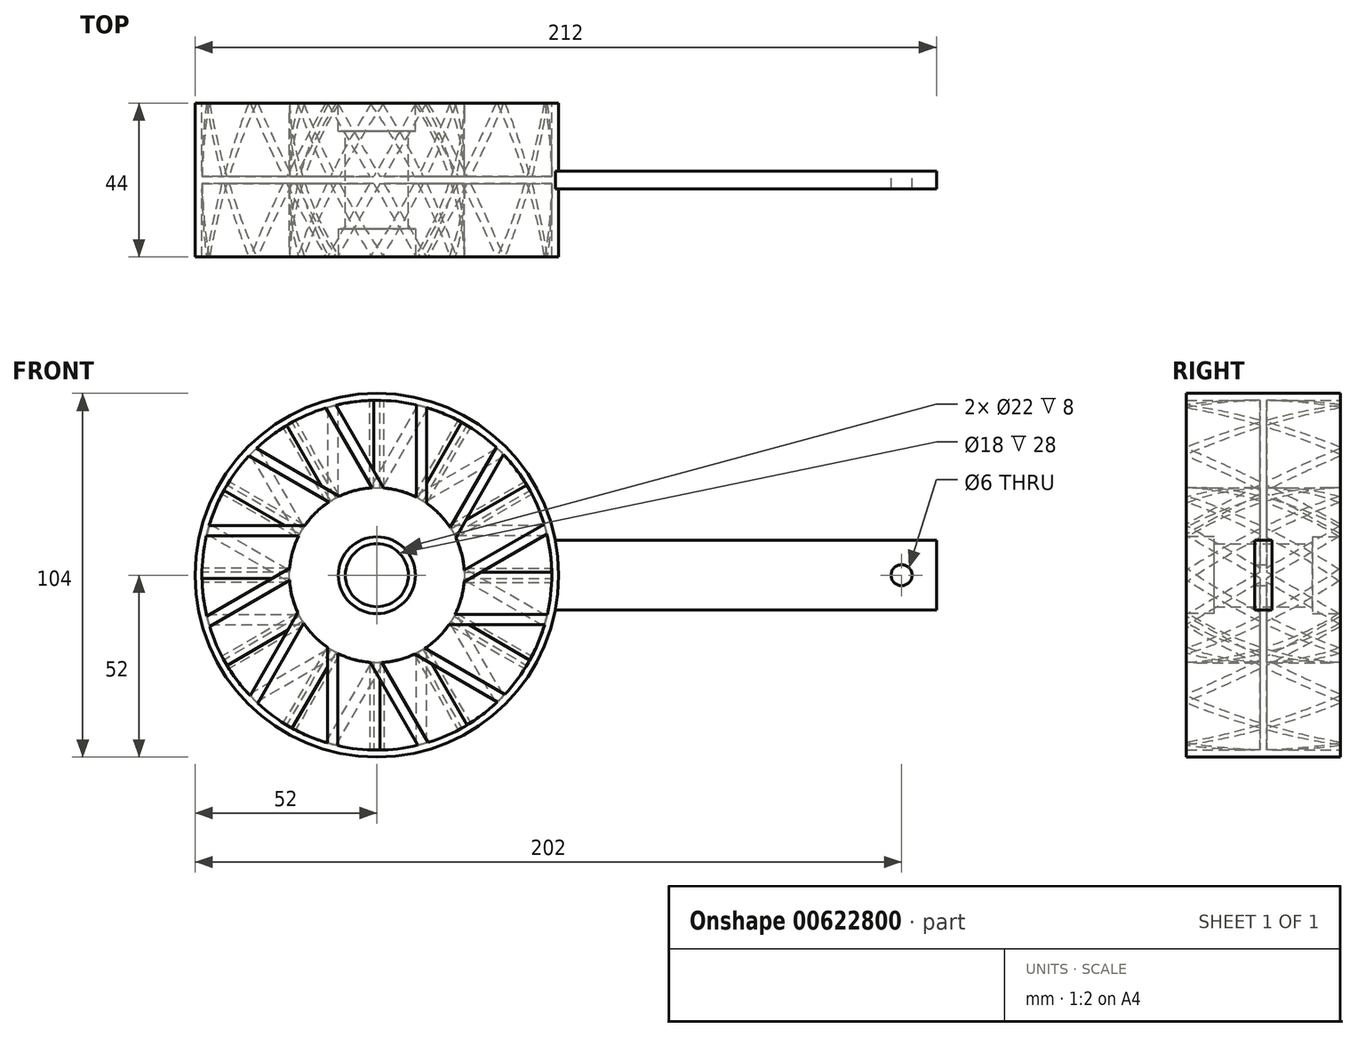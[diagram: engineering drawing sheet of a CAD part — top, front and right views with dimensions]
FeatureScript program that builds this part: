
annotation { "Feature Type Name" : "Feature", "Feature Type Description" : "" }
export const myFeature = defineFeature(function(context is Context, id is Id, definition is map)
    precondition{}
    {
        {
            var Q0;
            Q0=qCreatedBy(makeId("Front.planeOp"),FACE);
            var sketch = newSketch(context, id + "F0", { "sketchPlane" : qUnion([Q0])});
            skCircle(sketch, "E0", {"center": v(0, 0) * mm, "radius": 50 * mm});
            skCircle(sketch, "E1.0", {"center": v(0, 0) * mm, "radius": 52 * mm});
            skCircle(sketch, "E2", {"center": v(0, 0) * mm, "radius": 25 * mm});
            skCircle(sketch, "E3.0", {"center": v(0, 0) * mm, "radius": 23 * mm});
            skLineSegment(sketch, "E4", {"start": v(-23, 0) * mm, "end": v(-50, 0) * mm, "construction": true});
            skLineSegment(sketch, "E5.bottom", {"start": v(-57.83, -1.26) * mm, "end": v(-15.17, -1.26) * mm});
            skLineSegment(sketch, "E5.top", {"start": v(-57.83, 1.26) * mm, "end": v(-15.17, 1.26) * mm});
            skLineSegment(sketch, "E5.left", {"start": v(-57.83, -1.26) * mm, "end": v(-57.83, 1.26) * mm});
            skLineSegment(sketch, "E5.right", {"start": v(-15.17, -1.26) * mm, "end": v(-15.17, 1.26) * mm});
            skPoint(sketch, "E5.middle", {"position": v(-36.5, 0) * mm});
            skCircle(sketch, "E6", {"center": v(0, 0) * mm, "radius": 77.5 * mm});
            skCircle(sketch, "E7", {"center": v(0, 0) * mm, "radius": 9 * mm});
            skLineSegment(sketch, "E8", {"start": v(51.03, 10) * mm, "end": v(160, 10) * mm});
            skLineSegment(sketch, "E9", {"start": v(160, 10) * mm, "end": v(160, -10) * mm});
            skLineSegment(sketch, "E10", {"start": v(160, -10) * mm, "end": v(51.03, -10) * mm});
            skCircle(sketch, "E11", {"center": v(150, 0) * mm, "radius": 3 * mm});
            skSolve(sketch);
        }
        {
            var Q0;
            {var subQ0=sQuery(id+"F0.wireOp",EDGE,"E5.bottom");var subQ1=sQuery(id+"F0.wireOp",EDGE,"E0");var subQ2=makeQuery(id+"F0.imprint","INTERSECT",VERTEX,{"derivedFrom":[subQ1,subQ0]});Q0=makeQuery(id+"F0.imprint","IMPRINT",FACE,{"disambiguationData":[TD([[makeQuery(id+"F0.imprint","IMPRINT",EDGE,{"disambiguationData":[TD([[subQ2,-1.0]])],"derivedFrom":subQ1}),-1.0]])]});}
            var Q1;
            {var subQ0=sQuery(id+"F0.wireOp",EDGE,"E5.bottom");var subQ1=sQuery(id+"F0.wireOp",EDGE,"E0");var subQ2=makeQuery(id+"F0.imprint","INTERSECT",VERTEX,{"derivedFrom":[subQ1,subQ0]});Q1=makeQuery(id+"F0.imprint","IMPRINT",FACE,{"disambiguationData":[TD([[makeQuery(id+"F0.imprint","IMPRINT",EDGE,{"disambiguationData":[TD([[subQ2,1.0]])],"derivedFrom":subQ1}),-1.0]])]});}
            extrude(context, id + "F1", {"entities" : qUnion([Q0, Q1]), "depth" : 22 * mm, "offsetDistance" : 25 * mm, "hasSecondDirection" : true, "secondDirectionOppositeDirection" : true, "secondDirectionDepth" : 22 * mm});
        }
        {
            var Q0;
            {var subQ0=sQuery(id+"F0.wireOp",EDGE,"124578b7-64f7-4ebe-a5cb-b1fa8b997d8e.0");var subQ1=sQuery(id+"F0.wireOp",EDGE,"E0");var subQ2=makeQuery(id+"F0.imprint","INTERSECT",VERTEX,{"derivedFrom":[subQ1,subQ0]});Q0=makeQuery(id+"F0.imprint","IMPRINT",FACE,{"disambiguationData":[TD([[makeQuery(id+"F0.imprint","IMPRINT",EDGE,{"disambiguationData":[TD([[subQ2,1.0]])],"derivedFrom":subQ1}),1.0]])]});}
            var Q1;
            {var subQ5=sQuery(id+"F0.wireOp",EDGE,"E5.right");Q1=makeQuery(id+"F0.imprint","IMPRINT",FACE,{"disambiguationData":[TD([[makeQuery(id+"F0.imprint","IMPRINT",EDGE,{"derivedFrom":subQ5}),1.0]])]});}
            var Q2;
            {var subQ0=sQuery(id+"F0.wireOp",EDGE,"E5.right");Q2=makeQuery(id+"F0.imprint","IMPRINT",FACE,{"disambiguationData":[TD([[makeQuery(id+"F0.imprint","IMPRINT",EDGE,{"derivedFrom":subQ0}),-1.0]])]});}
            extrude(context, id + "F2", {"entities" : qUnion([Q0, Q1, Q2]), "operationType" : NewBodyOperationType.ADD, "depth" : 1 * mm, "offsetDistance" : 25 * mm, "hasSecondDirection" : true, "secondDirectionOppositeDirection" : true, "secondDirectionDepth" : 1 * mm});
        }
        {
            var Q0;
            Q0=makeQuery(id+"F0.imprint","IMPRINT",FACE,{"disambiguationData":[TD([[makeQuery(id+"F0.imprint","IMPRINT",EDGE,{"derivedFrom":sQuery(id+"F0.wireOp",EDGE,"E3.0")}),-1.0]])]});
            var Q1;
            {var subQ0=sQuery(id+"F0.wireOp",EDGE,"E5.right");Q1=makeQuery(id+"F0.imprint","IMPRINT",FACE,{"disambiguationData":[TD([[makeQuery(id+"F0.imprint","IMPRINT",EDGE,{"derivedFrom":subQ0}),-1.0]])]});}
            var Q2;
            {var subQ5=sQuery(id+"F0.wireOp",EDGE,"E5.right");Q2=makeQuery(id+"F0.imprint","IMPRINT",FACE,{"disambiguationData":[TD([[makeQuery(id+"F0.imprint","IMPRINT",EDGE,{"derivedFrom":subQ5}),1.0]])]});}
            extrude(context, id + "F3", {"entities" : qUnion([Q0, Q1, Q2]), "operationType" : NewBodyOperationType.ADD, "depth" : 22 * mm, "offsetDistance" : 25 * mm, "hasSecondDirection" : true, "secondDirectionOppositeDirection" : true, "secondDirectionDepth" : 22 * mm});
        }
        {
            var Q0;
            {var subQ5=sQuery(id+"F0.wireOp",EDGE,"E5.left");Q0=makeQuery(id+"F0.imprint","IMPRINT",FACE,{"disambiguationData":[TD([[makeQuery(id+"F0.imprint","IMPRINT",EDGE,{"derivedFrom":subQ5}),-1.0]])]});}
            var Q1;
            {var subQ0=sQuery(id+"F0.wireOp",EDGE,"E5.bottom");var subQ1=sQuery(id+"F0.wireOp",EDGE,"E0");var subQ2=makeQuery(id+"F0.imprint","INTERSECT",VERTEX,{"derivedFrom":[subQ1,subQ0]});Q1=makeQuery(id+"F0.imprint","IMPRINT",FACE,{"disambiguationData":[TD([[makeQuery(id+"F0.imprint","IMPRINT",EDGE,{"disambiguationData":[TD([[subQ2,1.0]])],"derivedFrom":subQ1}),-1.0]])]});}
            var Q2;
            {var subQ0=sQuery(id+"F0.wireOp",EDGE,"E5.bottom");var subQ1=sQuery(id+"F0.wireOp",EDGE,"E0");var subQ2=makeQuery(id+"F0.imprint","INTERSECT",VERTEX,{"derivedFrom":[subQ1,subQ0]});Q2=makeQuery(id+"F0.imprint","IMPRINT",FACE,{"disambiguationData":[TD([[makeQuery(id+"F0.imprint","IMPRINT",EDGE,{"disambiguationData":[TD([[subQ2,1.0]])],"derivedFrom":subQ1}),1.0]])]});}
            var Q3;
            {var subQ0=sQuery(id+"F0.wireOp",EDGE,"E5.bottom");var subQ1=sQuery(id+"F0.wireOp",EDGE,"E2");var subQ2=makeQuery(id+"F0.imprint","INTERSECT",VERTEX,{"derivedFrom":[subQ1,subQ0]});Q3=makeQuery(id+"F0.imprint","IMPRINT",FACE,{"disambiguationData":[TD([[makeQuery(id+"F0.imprint","IMPRINT",EDGE,{"disambiguationData":[TD([[subQ2,1.0]])],"derivedFrom":subQ1}),1.0]])]});}
            var Q4;
            {var subQ5=sQuery(id+"F0.wireOp",EDGE,"E5.right");Q4=makeQuery(id+"F0.imprint","IMPRINT",FACE,{"disambiguationData":[TD([[makeQuery(id+"F0.imprint","IMPRINT",EDGE,{"derivedFrom":subQ5}),1.0]])]});}
            extrude(context, id + "F4", {"entities" : qUnion([Q0, Q1, Q2, Q3, Q4]), "depth" : 28 * mm, "offsetDistance" : 25 * mm, "hasSecondDirection" : true, "secondDirectionOppositeDirection" : true, "secondDirectionDepth" : 28 * mm});
        }
        {
            var Q0;
            Q0=makeQuery(id+"F4.opExtrude","SWEPT_BODY",BODY,{"disambiguationData":[OSD([sQuery(id+"F0.wireOp",EDGE,"E5.bottom"),sQuery(id+"F0.wireOp",EDGE,"E5.top"),sQuery(id+"F0.wireOp",EDGE,"E5.left"),sQuery(id+"F0.wireOp",EDGE,"E5.right")])]});
            var Q1;
            Q1=sQuery(id+"F0.wireOp",EDGE,"E4");
            transform(context, id + "F5", {"entities" : qUnion([Q0]), "transformType" : TransformType.ROTATION, "transformAxis" : qUnion([Q1]), "angle" : 30 * degree, "makeCopy" : false});
        }
        {
            var Q0;
            {var subQ0=sQuery(id+"F0.wireOp",EDGE,"E5.left");Q0=makeQuery(id+"F0.imprint","IMPRINT",FACE,{"disambiguationData":[TD([[makeQuery(id+"F0.imprint","IMPRINT",EDGE,{"derivedFrom":subQ0}),1.0]])]});}
            var Q1;
            {var subQ5=sQuery(id+"F0.wireOp",EDGE,"E5.left");Q1=makeQuery(id+"F0.imprint","IMPRINT",FACE,{"disambiguationData":[TD([[makeQuery(id+"F0.imprint","IMPRINT",EDGE,{"derivedFrom":subQ5}),-1.0]])]});}
            extrude(context, id + "F6", {"entities" : qUnion([Q0, Q1]), "operationType" : NewBodyOperationType.REMOVE, "oppositeDirection" : true, "depth" : 25 * mm, "offsetDistance" : 25 * mm, "hasSecondDirection" : true, "secondDirectionOppositeDirection" : false, "secondDirectionDepth" : 25 * mm});
        }
        {
            var Q0;
            Q0=makeQuery(id+"F4.opExtrude","SWEPT_BODY",BODY,{"disambiguationData":[OSD([sQuery(id+"F0.wireOp",EDGE,"E5.bottom"),sQuery(id+"F0.wireOp",EDGE,"E5.top"),sQuery(id+"F0.wireOp",EDGE,"E5.left"),sQuery(id+"F0.wireOp",EDGE,"E5.right")])]});
            var Q1;
            Q1=sQuery(id+"F0.wireOp",EDGE,"E3.0");
            circularPattern(context, id + "F7", {"entities" : qUnion([Q0]), "axis" : qUnion([Q1]), "angle" : 360 * degree, "instanceCount" : 12, "equalSpace" : true});
        }
        {
            var Q0;
            Q0=qCreatedBy(makeId("Right.planeOp"),FACE);
            var sketch = newSketch(context, id + "F8", { "sketchPlane" : qUnion([Q0])});
            skLineSegment(sketch, "E12.bottom", {"start": v(22, 52) * mm, "end": v(-22, 52) * mm});
            skLineSegment(sketch, "E12.top", {"start": v(22, -52) * mm, "end": v(-22, -52) * mm});
            skLineSegment(sketch, "E12.left", {"start": v(22, 52) * mm, "end": v(22, -52) * mm});
            skLineSegment(sketch, "E12.right", {"start": v(-22, 52) * mm, "end": v(-22, -52) * mm});
            skPoint(sketch, "E12.middle", {"position": v(0, 0) * mm});
            skLineSegment(sketch, "E13.bottom", {"start": v(30, 60) * mm, "end": v(-30, 60) * mm});
            skLineSegment(sketch, "E13.top", {"start": v(30, -60) * mm, "end": v(-30, -60) * mm});
            skLineSegment(sketch, "E13.left", {"start": v(30, 60) * mm, "end": v(30, -60) * mm});
            skLineSegment(sketch, "E13.right", {"start": v(-30, 60) * mm, "end": v(-30, -60) * mm});
            skSolve(sketch);
        }
        {
            var Q0;
            Q0 = qSketchRegion(id + "F8", true);
            extrude(context, id + "F9", {"entities" : qUnion([Q0]), "operationType" : NewBodyOperationType.REMOVE, "endBound" : BoundingType.THROUGH_ALL, "oppositeDirection" : true, "depth" : 25 * mm, "offsetDistance" : 25 * mm, "hasSecondDirection" : true, "secondDirectionBound" : SecondDirectionBoundingType.THROUGH_ALL, "secondDirectionOppositeDirection" : false, "secondDirectionDepth" : 25 * mm});
        }
        {
            var Q0;
            Q0=makeQuery(id+"F1.opExtrude","SWEPT_BODY",BODY,{"disambiguationData":[OSD([sQuery(id+"F0.wireOp",EDGE,"E0"),sQuery(id+"F0.wireOp",EDGE,"E1.0")])]});
            var Q1;
            Q1=makeQuery(id+"F2.opExtrude","SWEPT_BODY",BODY,{"disambiguationData":[OSD([sQuery(id+"F0.wireOp",EDGE,"E3.0"),sQuery(id+"F0.wireOp",EDGE,"E7")])]});
            var Q2;
            Q2=makeQuery(id+"F4.opExtrude","SWEPT_BODY",BODY,{"disambiguationData":[OSD([sQuery(id+"F0.wireOp",EDGE,"E5.bottom"),sQuery(id+"F0.wireOp",EDGE,"E5.top"),sQuery(id+"F0.wireOp",EDGE,"E5.left"),sQuery(id+"F0.wireOp",EDGE,"E5.right")])]});
            var Q3;
            Q3=makeQuery(id+"F7.opPattern","COPY",BODY,{"derivedFrom":makeQuery(id+"F4.opExtrude","SWEPT_BODY",BODY,{"disambiguationData":[OSD([sQuery(id+"F0.wireOp",EDGE,"E5.bottom"),sQuery(id+"F0.wireOp",EDGE,"E5.top"),sQuery(id+"F0.wireOp",EDGE,"E5.left"),sQuery(id+"F0.wireOp",EDGE,"E5.right")])]}),"instanceName":"1"});
            var Q4;
            Q4=makeQuery(id+"F7.opPattern","COPY",BODY,{"derivedFrom":makeQuery(id+"F4.opExtrude","SWEPT_BODY",BODY,{"disambiguationData":[OSD([sQuery(id+"F0.wireOp",EDGE,"E5.bottom"),sQuery(id+"F0.wireOp",EDGE,"E5.top"),sQuery(id+"F0.wireOp",EDGE,"E5.left"),sQuery(id+"F0.wireOp",EDGE,"E5.right")])]}),"instanceName":"2"});
            var Q5;
            Q5=makeQuery(id+"F7.opPattern","COPY",BODY,{"derivedFrom":makeQuery(id+"F4.opExtrude","SWEPT_BODY",BODY,{"disambiguationData":[OSD([sQuery(id+"F0.wireOp",EDGE,"E5.bottom"),sQuery(id+"F0.wireOp",EDGE,"E5.top"),sQuery(id+"F0.wireOp",EDGE,"E5.left"),sQuery(id+"F0.wireOp",EDGE,"E5.right")])]}),"instanceName":"3"});
            var Q6;
            Q6=makeQuery(id+"F7.opPattern","COPY",BODY,{"derivedFrom":makeQuery(id+"F4.opExtrude","SWEPT_BODY",BODY,{"disambiguationData":[OSD([sQuery(id+"F0.wireOp",EDGE,"E5.bottom"),sQuery(id+"F0.wireOp",EDGE,"E5.top"),sQuery(id+"F0.wireOp",EDGE,"E5.left"),sQuery(id+"F0.wireOp",EDGE,"E5.right")])]}),"instanceName":"4"});
            var Q7;
            Q7=makeQuery(id+"F7.opPattern","COPY",BODY,{"derivedFrom":makeQuery(id+"F4.opExtrude","SWEPT_BODY",BODY,{"disambiguationData":[OSD([sQuery(id+"F0.wireOp",EDGE,"E5.bottom"),sQuery(id+"F0.wireOp",EDGE,"E5.top"),sQuery(id+"F0.wireOp",EDGE,"E5.left"),sQuery(id+"F0.wireOp",EDGE,"E5.right")])]}),"instanceName":"5"});
            var Q8;
            Q8=makeQuery(id+"F7.opPattern","COPY",BODY,{"derivedFrom":makeQuery(id+"F4.opExtrude","SWEPT_BODY",BODY,{"disambiguationData":[OSD([sQuery(id+"F0.wireOp",EDGE,"E5.bottom"),sQuery(id+"F0.wireOp",EDGE,"E5.top"),sQuery(id+"F0.wireOp",EDGE,"E5.left"),sQuery(id+"F0.wireOp",EDGE,"E5.right")])]}),"instanceName":"6"});
            var Q9;
            Q9=makeQuery(id+"F7.opPattern","COPY",BODY,{"derivedFrom":makeQuery(id+"F4.opExtrude","SWEPT_BODY",BODY,{"disambiguationData":[OSD([sQuery(id+"F0.wireOp",EDGE,"E5.bottom"),sQuery(id+"F0.wireOp",EDGE,"E5.top"),sQuery(id+"F0.wireOp",EDGE,"E5.left"),sQuery(id+"F0.wireOp",EDGE,"E5.right")])]}),"instanceName":"7"});
            var Q10;
            Q10=makeQuery(id+"F7.opPattern","COPY",BODY,{"derivedFrom":makeQuery(id+"F4.opExtrude","SWEPT_BODY",BODY,{"disambiguationData":[OSD([sQuery(id+"F0.wireOp",EDGE,"E5.bottom"),sQuery(id+"F0.wireOp",EDGE,"E5.top"),sQuery(id+"F0.wireOp",EDGE,"E5.left"),sQuery(id+"F0.wireOp",EDGE,"E5.right")])]}),"instanceName":"8"});
            var Q11;
            Q11=makeQuery(id+"F7.opPattern","COPY",BODY,{"derivedFrom":makeQuery(id+"F4.opExtrude","SWEPT_BODY",BODY,{"disambiguationData":[OSD([sQuery(id+"F0.wireOp",EDGE,"E5.bottom"),sQuery(id+"F0.wireOp",EDGE,"E5.top"),sQuery(id+"F0.wireOp",EDGE,"E5.left"),sQuery(id+"F0.wireOp",EDGE,"E5.right")])]}),"instanceName":"9"});
            var Q12;
            Q12=makeQuery(id+"F7.opPattern","COPY",BODY,{"derivedFrom":makeQuery(id+"F4.opExtrude","SWEPT_BODY",BODY,{"disambiguationData":[OSD([sQuery(id+"F0.wireOp",EDGE,"E5.bottom"),sQuery(id+"F0.wireOp",EDGE,"E5.top"),sQuery(id+"F0.wireOp",EDGE,"E5.left"),sQuery(id+"F0.wireOp",EDGE,"E5.right")])]}),"instanceName":"10"});
            var Q13;
            Q13=makeQuery(id+"F7.opPattern","COPY",BODY,{"derivedFrom":makeQuery(id+"F4.opExtrude","SWEPT_BODY",BODY,{"disambiguationData":[OSD([sQuery(id+"F0.wireOp",EDGE,"E5.bottom"),sQuery(id+"F0.wireOp",EDGE,"E5.top"),sQuery(id+"F0.wireOp",EDGE,"E5.left"),sQuery(id+"F0.wireOp",EDGE,"E5.right")])]}),"instanceName":"11"});
            booleanBodies(context, id + "F10", {"operationType" : BooleanOperationType.UNION, "tools" : qUnion([Q0, Q1, Q2, Q3, Q4, Q5, Q6, Q7, Q8, Q9, Q10, Q11, Q12, Q13])});
        }
        {
            var Q0;
            {var subQ0=sQuery(id+"F0.wireOp",EDGE,"E9");Q0=makeQuery(id+"F0.imprint","IMPRINT",FACE,{"disambiguationData":[TD([[makeQuery(id+"F0.imprint","IMPRINT",EDGE,{"derivedFrom":subQ0}),-1.0]])]});}
            var Q1;
            {var subQ0=sQuery(id+"F0.wireOp",EDGE,"E8");var subQ1=sQuery(id+"F0.wireOp",EDGE,"E1.0");var subQ2=makeQuery(id+"F0.imprint","INTERSECT",VERTEX,{"derivedFrom":[subQ1,subQ0]});Q1=makeQuery(id+"F0.imprint","IMPRINT",FACE,{"disambiguationData":[TD([[makeQuery(id+"F0.imprint","IMPRINT",EDGE,{"disambiguationData":[TD([[subQ2,1.0]])],"derivedFrom":subQ1}),-1.0]])]});}
            extrude(context, id + "F11", {"entities" : qUnion([Q0, Q1]), "operationType" : NewBodyOperationType.ADD, "endBound" : BoundingType.SYMMETRIC, "depth" : 5 * mm, "offsetDistance" : 25 * mm});
        }
        {
            var Q0;
            {var subQ0=makeQuery(id+"F4.opExtrude","SWEPT_FACE",FACE,{"disambiguationData":[OSD([sQuery(id+"F0.wireOp",EDGE,"E5.right")])]});var subQ3=sQuery(id+"F0.wireOp",EDGE,"E1.0");var subQ5=makeQuery(id+"F4.opExtrude","SWEPT_FACE",FACE,{"disambiguationData":[OSD([sQuery(id+"F0.wireOp",EDGE,"E5.bottom")])]});var subQ7=makeQuery(id+"F9.opExtrude","SWEPT_FACE",FACE,{"disambiguationData":[OSD([sQuery(id+"F8.wireOp",EDGE,"E12.right")])]});Q0=makeQuery(id+"F10.opBoolean","MERGE",FACE,{"derivedFrom":[makeQuery(id+"F1.opExtrude","CAP_FACE",FACE,{"disambiguationData":[OSD([sQuery(id+"F0.wireOp",EDGE,"E0"),subQ3])],"isStart":false}),makeQuery(id+"F3.opExtrude","CAP_FACE",FACE,{"disambiguationData":[OSD([sQuery(id+"F0.wireOp",EDGE,"E2"),sQuery(id+"F0.wireOp",EDGE,"E7")])],"isStart":false}),makeQuery(id+"F9.boolean.opBoolean","COPY",FACE,{"disambiguationData":[TD([subQ5])],"derivedFrom":subQ7}),makeQuery(id+"F9.boolean.opBoolean","COPY",FACE,{"disambiguationData":[TD([makeQuery(id+"F7.opPattern","COPY",FACE,{"derivedFrom":subQ0,"instanceName":"1"})])],"derivedFrom":subQ7}),makeQuery(id+"F9.boolean.opBoolean","COPY",FACE,{"disambiguationData":[TD([makeQuery(id+"F7.opPattern","COPY",FACE,{"derivedFrom":subQ0,"instanceName":"2"})])],"derivedFrom":subQ7}),makeQuery(id+"F9.boolean.opBoolean","COPY",FACE,{"disambiguationData":[TD([makeQuery(id+"F7.opPattern","COPY",FACE,{"derivedFrom":subQ0,"instanceName":"3"})])],"derivedFrom":subQ7}),makeQuery(id+"F9.boolean.opBoolean","COPY",FACE,{"disambiguationData":[TD([makeQuery(id+"F7.opPattern","COPY",FACE,{"derivedFrom":subQ0,"instanceName":"4"})])],"derivedFrom":subQ7}),makeQuery(id+"F9.boolean.opBoolean","COPY",FACE,{"disambiguationData":[TD([makeQuery(id+"F7.opPattern","COPY",FACE,{"derivedFrom":subQ0,"instanceName":"5"})])],"derivedFrom":subQ7}),makeQuery(id+"F9.boolean.opBoolean","COPY",FACE,{"disambiguationData":[TD([makeQuery(id+"F7.opPattern","COPY",FACE,{"derivedFrom":subQ0,"instanceName":"6"})])],"derivedFrom":subQ7}),makeQuery(id+"F9.boolean.opBoolean","COPY",FACE,{"disambiguationData":[TD([makeQuery(id+"F7.opPattern","COPY",FACE,{"derivedFrom":subQ0,"instanceName":"7"})])],"derivedFrom":subQ7}),makeQuery(id+"F9.boolean.opBoolean","COPY",FACE,{"disambiguationData":[TD([makeQuery(id+"F7.opPattern","COPY",FACE,{"derivedFrom":subQ0,"instanceName":"8"})])],"derivedFrom":subQ7}),makeQuery(id+"F9.boolean.opBoolean","COPY",FACE,{"disambiguationData":[TD([makeQuery(id+"F7.opPattern","COPY",FACE,{"derivedFrom":subQ0,"instanceName":"9"})])],"derivedFrom":subQ7}),makeQuery(id+"F9.boolean.opBoolean","COPY",FACE,{"disambiguationData":[TD([makeQuery(id+"F7.opPattern","COPY",FACE,{"derivedFrom":subQ0,"instanceName":"10"})])],"derivedFrom":subQ7}),makeQuery(id+"F9.boolean.opBoolean","COPY",FACE,{"disambiguationData":[TD([makeQuery(id+"F7.opPattern","COPY",FACE,{"derivedFrom":subQ0,"instanceName":"11"})])],"derivedFrom":subQ7})]});}
            var sketch = newSketch(context, id + "F12", { "sketchPlane" : qUnion([Q0])});
            skCircle(sketch, "E14", {"center": v(0, 0) * mm, "radius": 11 * mm});
            skSolve(sketch);
        }
        {
            var Q0;
            Q0=makeQuery(id+"F12.imprint","IMPRINT",FACE,{"disambiguationData":[TD([[makeQuery(id+"F12.imprint","IMPRINT",EDGE,{"derivedFrom":sQuery(id+"F12.wireOp",EDGE,"E14")}),1.0]])]});
            extrude(context, id + "F13", {"entities" : qUnion([Q0]), "operationType" : NewBodyOperationType.REMOVE, "oppositeDirection" : true, "depth" : 8 * mm, "offsetDistance" : 25 * mm});
        }
        {
            var Q0;
            {var subQ0=makeQuery(id+"F4.opExtrude","SWEPT_FACE",FACE,{"disambiguationData":[OSD([sQuery(id+"F0.wireOp",EDGE,"E5.right")])]});var subQ3=sQuery(id+"F0.wireOp",EDGE,"E1.0");var subQ5=makeQuery(id+"F4.opExtrude","SWEPT_FACE",FACE,{"disambiguationData":[OSD([sQuery(id+"F0.wireOp",EDGE,"E5.bottom")])]});var subQ7=makeQuery(id+"F9.opExtrude","SWEPT_FACE",FACE,{"disambiguationData":[OSD([sQuery(id+"F8.wireOp",EDGE,"E12.left")])]});Q0=makeQuery(id+"F10.opBoolean","MERGE",FACE,{"derivedFrom":[makeQuery(id+"F1.opExtrude","CAP_FACE",FACE,{"disambiguationData":[OSD([sQuery(id+"F0.wireOp",EDGE,"E0"),subQ3])],"isStart":true}),makeQuery(id+"F3.opExtrude","CAP_FACE",FACE,{"disambiguationData":[OSD([sQuery(id+"F0.wireOp",EDGE,"E2"),sQuery(id+"F0.wireOp",EDGE,"E7")])],"isStart":true}),makeQuery(id+"F9.boolean.opBoolean","COPY",FACE,{"disambiguationData":[TD([subQ5])],"derivedFrom":subQ7}),makeQuery(id+"F9.boolean.opBoolean","COPY",FACE,{"disambiguationData":[TD([makeQuery(id+"F7.opPattern","COPY",FACE,{"derivedFrom":subQ0,"instanceName":"1"})])],"derivedFrom":subQ7}),makeQuery(id+"F9.boolean.opBoolean","COPY",FACE,{"disambiguationData":[TD([makeQuery(id+"F7.opPattern","COPY",FACE,{"derivedFrom":subQ0,"instanceName":"2"})])],"derivedFrom":subQ7}),makeQuery(id+"F9.boolean.opBoolean","COPY",FACE,{"disambiguationData":[TD([makeQuery(id+"F7.opPattern","COPY",FACE,{"derivedFrom":subQ0,"instanceName":"3"})])],"derivedFrom":subQ7}),makeQuery(id+"F9.boolean.opBoolean","COPY",FACE,{"disambiguationData":[TD([makeQuery(id+"F7.opPattern","COPY",FACE,{"derivedFrom":subQ0,"instanceName":"4"})])],"derivedFrom":subQ7}),makeQuery(id+"F9.boolean.opBoolean","COPY",FACE,{"disambiguationData":[TD([makeQuery(id+"F7.opPattern","COPY",FACE,{"derivedFrom":subQ0,"instanceName":"5"})])],"derivedFrom":subQ7}),makeQuery(id+"F9.boolean.opBoolean","COPY",FACE,{"disambiguationData":[TD([makeQuery(id+"F7.opPattern","COPY",FACE,{"derivedFrom":subQ0,"instanceName":"6"})])],"derivedFrom":subQ7}),makeQuery(id+"F9.boolean.opBoolean","COPY",FACE,{"disambiguationData":[TD([makeQuery(id+"F7.opPattern","COPY",FACE,{"derivedFrom":subQ0,"instanceName":"7"})])],"derivedFrom":subQ7}),makeQuery(id+"F9.boolean.opBoolean","COPY",FACE,{"disambiguationData":[TD([makeQuery(id+"F7.opPattern","COPY",FACE,{"derivedFrom":subQ0,"instanceName":"8"})])],"derivedFrom":subQ7}),makeQuery(id+"F9.boolean.opBoolean","COPY",FACE,{"disambiguationData":[TD([makeQuery(id+"F7.opPattern","COPY",FACE,{"derivedFrom":subQ0,"instanceName":"9"})])],"derivedFrom":subQ7}),makeQuery(id+"F9.boolean.opBoolean","COPY",FACE,{"disambiguationData":[TD([makeQuery(id+"F7.opPattern","COPY",FACE,{"derivedFrom":subQ0,"instanceName":"10"})])],"derivedFrom":subQ7}),makeQuery(id+"F9.boolean.opBoolean","COPY",FACE,{"disambiguationData":[TD([makeQuery(id+"F7.opPattern","COPY",FACE,{"derivedFrom":subQ0,"instanceName":"11"})])],"derivedFrom":subQ7})]});}
            var sketch = newSketch(context, id + "F14", { "sketchPlane" : qUnion([Q0])});
            skCircle(sketch, "E15", {"center": v(0, 0) * mm, "radius": 11 * mm});
            skSolve(sketch);
        }
        {
            var Q0;
            Q0=makeQuery(id+"F14.imprint","IMPRINT",FACE,{"disambiguationData":[TD([[makeQuery(id+"F14.imprint","IMPRINT",EDGE,{"derivedFrom":sQuery(id+"F14.wireOp",EDGE,"E15")}),1.0]])]});
            extrude(context, id + "F15", {"entities" : qUnion([Q0]), "operationType" : NewBodyOperationType.REMOVE, "oppositeDirection" : true, "depth" : 8 * mm, "offsetDistance" : 25 * mm});
        }
    });
